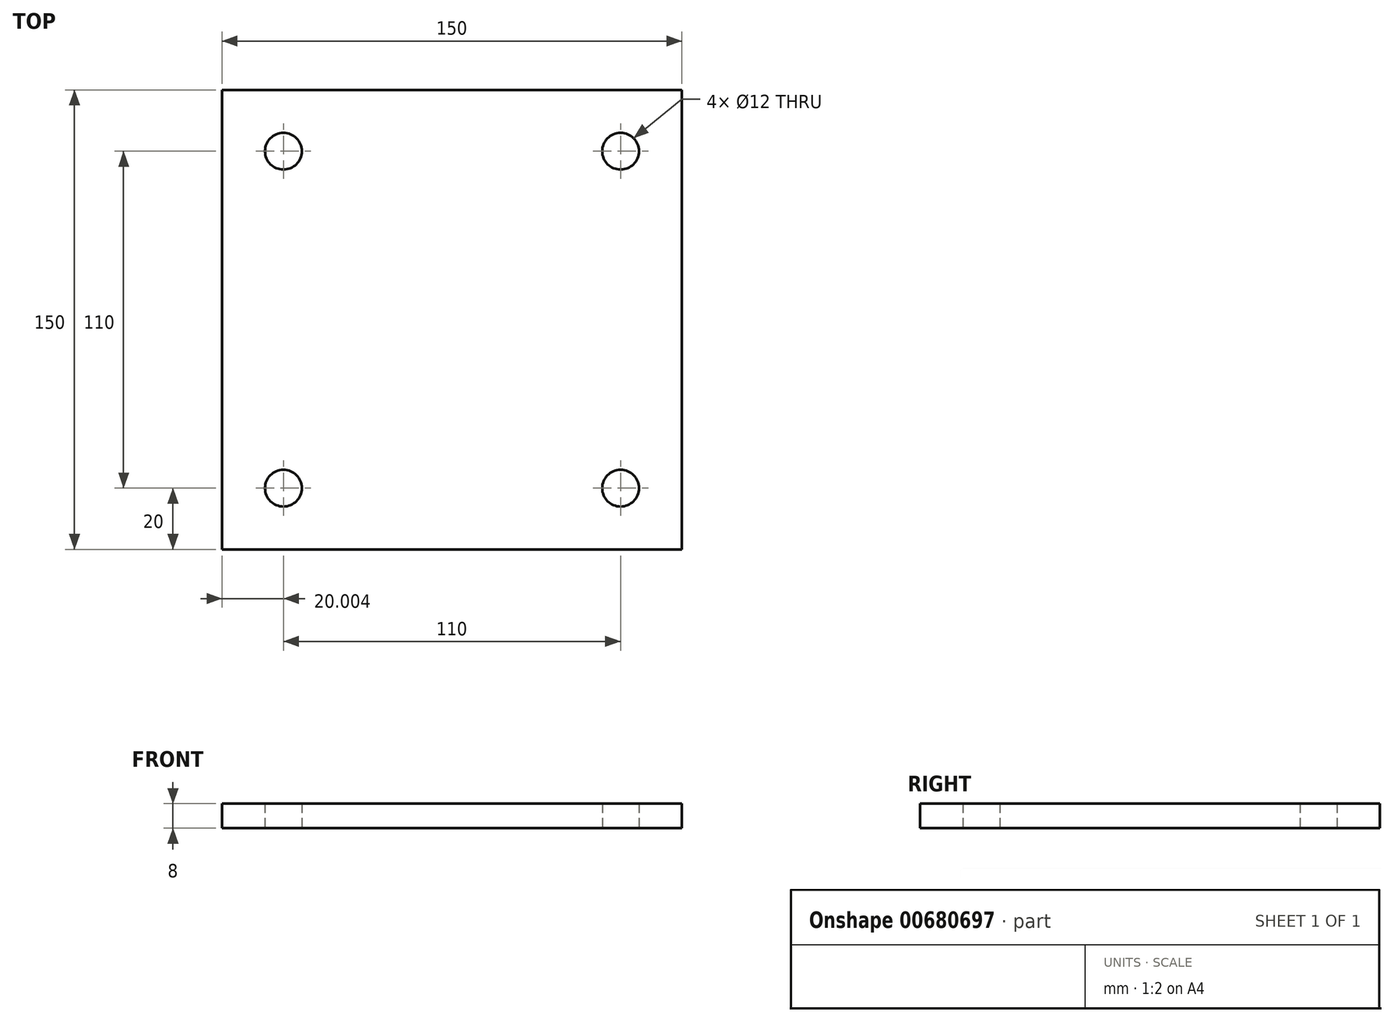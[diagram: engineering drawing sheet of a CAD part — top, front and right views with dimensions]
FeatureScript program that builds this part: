
annotation { "Feature Type Name" : "Feature", "Feature Type Description" : "" }
export const myFeature = defineFeature(function(context is Context, id is Id, definition is map)
    precondition{}
    {
        {
            var Q0;
            Q0=qCreatedBy(makeId("Top.planeOp"),FACE);
            var sketch = newSketch(context, id + "F0", { "sketchPlane" : qUnion([Q0])});
            skLineSegment(sketch, "E0.bottom", {"start": v(77.1, 75) * mm, "end": v(-72.9, 75) * mm});
            skLineSegment(sketch, "E0.top", {"start": v(77.1, -75) * mm, "end": v(-72.9, -75) * mm});
            skLineSegment(sketch, "E0.left", {"start": v(77.1, 75) * mm, "end": v(77.1, -75) * mm});
            skLineSegment(sketch, "E0.right", {"start": v(-72.9, 75) * mm, "end": v(-72.9, -75) * mm});
            skPoint(sketch, "E0.middle", {"position": v(2.1, 0) * mm});
            skCircle(sketch, "E1", {"center": v(-52.9, 55) * mm, "radius": 6 * mm});
            skCircle(sketch, "E2", {"center": v(57.1, 55) * mm, "radius": 6 * mm});
            skCircle(sketch, "E3", {"center": v(-52.9, -55) * mm, "radius": 6 * mm});
            skCircle(sketch, "E4", {"center": v(57.1, -55) * mm, "radius": 6 * mm});
            skSolve(sketch);
        }
        {
            var Q0;
            Q0=makeQuery(id+"F0.imprint","IMPRINT",FACE,{"disambiguationData":[TD([[makeQuery(id+"F0.imprint","IMPRINT",EDGE,{"derivedFrom":sQuery(id+"F0.wireOp",EDGE,"E0.bottom")}),1.0]])]});
            extrude(context, id + "F1", {"entities" : qUnion([Q0]), "depth" : 8 * mm, "offsetDistance" : 25 * mm});
        }
    });
